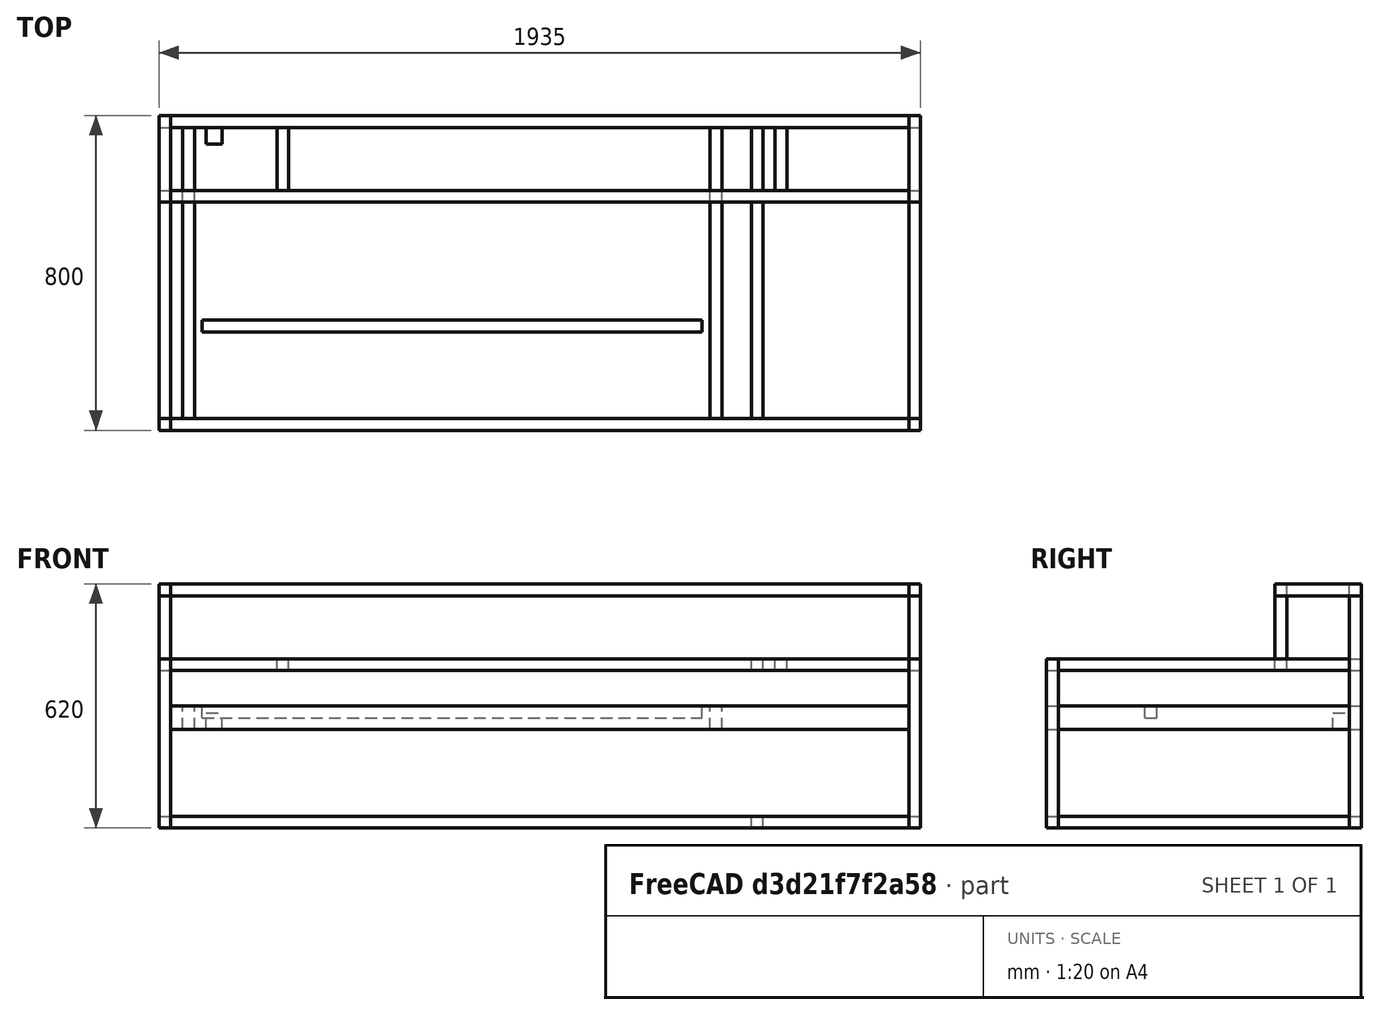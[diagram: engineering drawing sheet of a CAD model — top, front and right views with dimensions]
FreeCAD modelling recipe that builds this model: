
FCSTD DOCUMENT
Label: photonsaw-chassis-1
objects: Part::Box×29, App::DocumentObjectGroup×7
note: 29 computed .brp shape members not serialized (recipe doc carries the construction recipe); baked Part::Feature solids carry a one-line shape summary decoded from their .brp

FEATURE [Part::Box] Box  label="Left Rear pillar"
  Height = 590
  Length = 30
  Placement = pos=(0,770,0) rot=(0,0,1;0rad)
  Width = 30
FEATURE [Part::Box] Box001  label="Left Front pillar"
  Height = 430
  Length = 30
  Width = 30
FEATURE [Part::Box] Box002  label="Left Bottom beam"
  Height = 30
  Length = 30
  Placement = pos=(0,30,0) rot=(0,0,1;0rad)
  Width = 740
FEATURE [Part::Box] Box002001  label="Left Top beam"
  Height = 30
  Length = 30
  Placement = pos=(0,30,400) rot=(0,0,1;0rad)
  Width = 740
FEATURE [App::DocumentObjectGroup] Group  label="Left"
  Group = -> [Box,Box001,Box002,Box002001]
FEATURE [Part::Box] Box002002  label="Right Rear pillar"
  Height = 590
  Length = 30
  Placement = pos=(1905,770,0) rot=(0,0,1;0rad)
  Width = 30
FEATURE [Part::Box] Box001001  label="Right Front pillar"
  Height = 430
  Length = 30
  Placement = pos=(1905,0,0) rot=(0,0,1;0rad)
  Width = 30
FEATURE [Part::Box] Box002003  label="Right Bottom beam"
  Height = 30
  Length = 30
  Placement = pos=(1905,30,0) rot=(0,0,1;0rad)
  Width = 740
FEATURE [Part::Box] Box002001001  label="Right Top beam"
  Height = 30
  Length = 30
  Placement = pos=(1905,30,400) rot=(0,0,1;0rad)
  Width = 740
FEATURE [App::DocumentObjectGroup] Group001  label="Right"
  Group = -> [Box002002,Box001001,Box002003,Box002001001]
FEATURE [Part::Box] Box002001002  label="Bottom Front beam"
  Height = 30
  Length = 1875
  Placement = pos=(30,0,0) rot=(0,0,1;0rad)
  Width = 30
FEATURE [Part::Box] Box002001002001  label="Bottom Rear beam"
  Height = 30
  Length = 1875
  Placement = pos=(30,770,0) rot=(0,0,1;0rad)
  Width = 30
FEATURE [Part::Box] Box002001002001001  label="Top Rear beam"
  Height = 30
  Length = 1875
  Placement = pos=(30,770,400) rot=(0,0,1;0rad)
  Width = 30
FEATURE [Part::Box] Box002001002001002  label="Top Front beam"
  Height = 30
  Length = 1875
  Placement = pos=(30,0,400) rot=(0,0,1;0rad)
  Width = 30
FEATURE [Part::Box] Box002001002001001001  label="Top Mid beam"
  Height = 30
  Length = 1875
  Placement = pos=(30,580,400) rot=(0,0,1;0rad)
  Width = 30
FEATURE [Part::Box] Box002003001  label="Bottom Firewall beam"
  Height = 30
  Length = 30
  Placement = pos=(1505,30,0) rot=(0,0,1;0rad)
  Width = 740
FEATURE [App::DocumentObjectGroup] Group002  label="Bottom"
  Group = -> [Box002001002,Box002001002001,Box002003001]
FEATURE [Part::Box] Box002001002001001002  label="Laser box rear beam"
  Height = 30
  Length = 1875
  Placement = pos=(30,770,590) rot=(0,0,1;0rad)
  Width = 30
FEATURE [Part::Box] Box002001002001001002001  label="Laser box front beam"
  Height = 30
  Length = 1875
  Placement = pos=(30,580,590) rot=(0,0,1;0rad)
  Width = 30
FEATURE [Part::Box] Box002001002001001002002  label="Laser box left pillar"
  Height = 160
  Length = 30
  Placement = pos=(0,580,430) rot=(0,0,1;0rad)
  Width = 30
FEATURE [Part::Box] Box002001002001001002002001  label="Laser box right pillar"
  Height = 160
  Length = 30
  Placement = pos=(1905,580,430) rot=(0,0,1;0rad)
  Width = 30
FEATURE [Part::Box] Box002001002001001002002002  label="laser box left top"
  Height = 30
  Length = 30
  Placement = pos=(0,580,590) rot=(0,0,1;0rad)
  Width = 220
FEATURE [Part::Box] Box002001002001001002002002001  label="laser box right top"
  Height = 30
  Length = 30
  Placement = pos=(1905,580,590) rot=(0,0,1;0rad)
  Width = 220
FEATURE [Part::Box] Box002001002001001002002002002  label="laser box floor left"
  Height = 30
  Length = 30
  Placement = pos=(300,610,400) rot=(0,0,1;0rad)
  Width = 160
FEATURE [Part::Box] Box002001002001001002002002002001  label="laser box floor right"
  Height = 30
  Length = 30
  Placement = pos=(1565,610,400) rot=(0,0,1;0rad)
  Width = 160
FEATURE [App::DocumentObjectGroup] Group004  label="Laser box"
  Group = -> [Box002001002001001002,Box002001002001001002001,Box002001002001001002002,Box002001002001001002002001,Box002001002001001002002002,Box002001002001001002002002001,Box002001002001001002002002002,Box002001002001001002002002002001]
FEATURE [Part::Box] Box002001002001001002002002002001001  label="Top Firewall front beam"
  Height = 30
  Length = 30
  Placement = pos=(1505,30,400) rot=(0,0,1;0rad)
  Width = 550
FEATURE [App::DocumentObjectGroup] Group003  label="Top"
  Group = -> [Box002001002001001,Box002001002001002,Box002001002001001001,Box002001002001001002002002002001001]
FEATURE [Part::Box] Box002001002001002001  label="Motion front beam"
  Height = 60
  Length = 1875
  Placement = pos=(30,0,250) rot=(0,0,1;0rad)
  Width = 30
FEATURE [Part::Box] Box002001002001002001001  label="Motion rear beam"
  Height = 60
  Length = 1875
  Placement = pos=(30,770,250) rot=(0,0,1;0rad)
  Width = 30
FEATURE [Part::Box] Box002001002001001002002002002001002  label="Motion Left Y axis"
  Height = 60
  Length = 30
  Placement = pos=(60,30,250) rot=(0,0,1;0rad)
  Width = 740
FEATURE [Part::Box] Box002001002001001002002002002001002001  label="Motion Right Y axis"
  Height = 60
  Length = 30
  Placement = pos=(1400,30,250) rot=(0,0,1;0rad)
  Width = 740
FEATURE [Part::Box] Box002001002001001002002002002001002002  label="Motion X axis"
  Height = 30
  Length = 1270
  Placement = pos=(110,250,280) rot=(0,0,1;0rad)
  Width = 30
FEATURE [App::DocumentObjectGroup] Group005  label="Motion"
  Group = -> [Box002001002001002001,Box002001002001002001001,Box002001002001001002002002002001002,Box002001002001001002002002002001002001,Box002001002001001002002002002001002002]
FEATURE [Part::Box] Box002001002001001002002002002001002003  label="Y Motor Left"
  Height = 42
  Length = 40
  Placement = pos=(120,728,250) rot=(0,0,1;0rad)
  Width = 42
FEATURE [App::DocumentObjectGroup] Group006  label="Hardware"
  Group = -> [Box002001002001001002002002002001002003]
